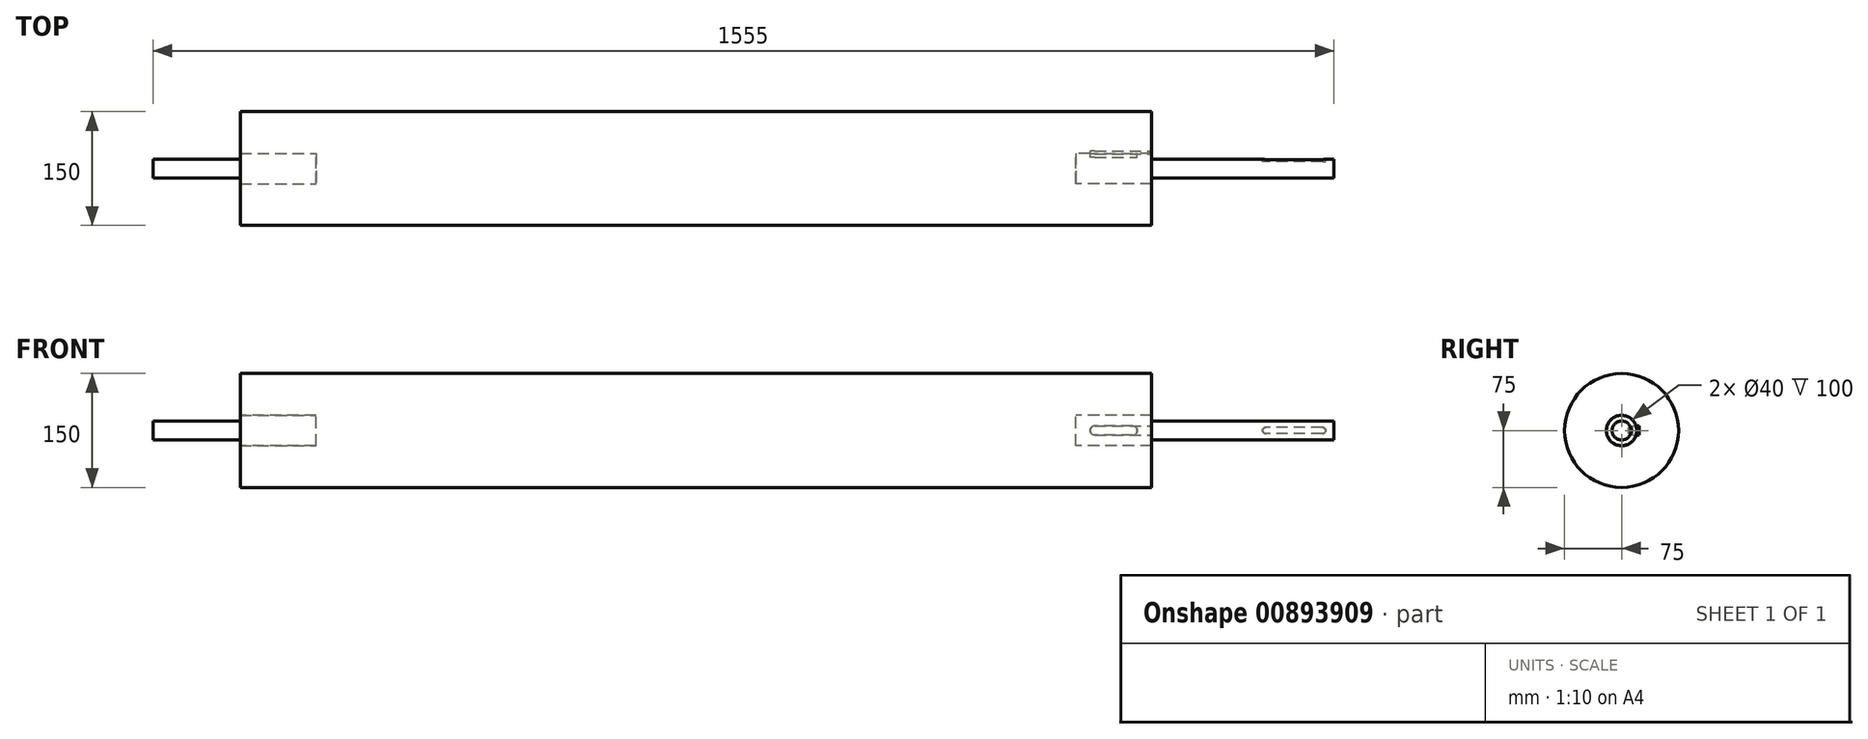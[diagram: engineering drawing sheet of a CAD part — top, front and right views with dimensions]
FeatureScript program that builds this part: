
annotation { "Feature Type Name" : "Feature", "Feature Type Description" : "" }
export const myFeature = defineFeature(function(context is Context, id is Id, definition is map)
    precondition{}
    {
        {
            var Q0;
            Q0=qCreatedBy(makeId("Right.planeOp"),FACE);
            var sketch = newSketch(context, id + "F0", { "sketchPlane" : qUnion([Q0])});
            skCircle(sketch, "E0", {"center": v(0, 0) * mm, "radius": 75 * mm});
            skSolve(sketch);
        }
        {
            var Q0;
            Q0 = qSketchRegion(id + "F0", true);
            extrude(context, id + "F1", {"entities" : qUnion([Q0]), "endBound" : BoundingType.SYMMETRIC, "depth" : 1200 * mm, "offsetDistance" : 25 * mm});
        }
        {
            var Q0;
            Q0=makeQuery(id+"F1.opExtrude","CAP_FACE",FACE,{"disambiguationData":[OSD([sQuery(id+"F0.wireOp",EDGE,"E0")])],"isStart":false});
            var sketch = newSketch(context, id + "F2", { "sketchPlane" : qUnion([Q0])});
            skCircle(sketch, "E1", {"center": v(0, 0) * mm, "radius": 20 * mm});
            skSolve(sketch);
        }
        {
            var Q0;
            Q0 = qSketchRegion(id + "F2", true);
            extrude(context, id + "F3", {"entities" : qUnion([Q0]), "operationType" : NewBodyOperationType.REMOVE, "oppositeDirection" : true, "depth" : 100 * mm, "offsetDistance" : 25 * mm});
        }
        {
            var Q0;
            Q0=makeQuery(id+"F1.opExtrude","CAP_FACE",FACE,{"disambiguationData":[OSD([sQuery(id+"F0.wireOp",EDGE,"E0")])],"isStart":true});
            var sketch = newSketch(context, id + "F4", { "sketchPlane" : qUnion([Q0])});
            skCircle(sketch, "E2", {"center": v(0, 0) * mm, "radius": 20 * mm});
            skSolve(sketch);
        }
        {
            var Q0;
            Q0 = qSketchRegion(id + "F4", true);
            extrude(context, id + "F5", {"entities" : qUnion([Q0]), "operationType" : NewBodyOperationType.REMOVE, "oppositeDirection" : true, "depth" : 100 * mm, "offsetDistance" : 25 * mm});
        }
        {
            var Q0;
            Q0=makeQuery(id+"F1.opExtrude","CAP_FACE",FACE,{"disambiguationData":[OSD([sQuery(id+"F0.wireOp",EDGE,"E0")])],"isStart":false});
            var sketch = newSketch(context, id + "F6", { "sketchPlane" : qUnion([Q0])});
            skLineSegment(sketch, "E3.bottom", {"start": v(19.08, 6) * mm, "end": v(23.3, 6) * mm});
            skLineSegment(sketch, "E3.top", {"start": v(19.08, -6) * mm, "end": v(23.3, -6) * mm});
            skLineSegment(sketch, "E3.left", {"start": v(19.08, 6) * mm, "end": v(19.08, -6) * mm});
            skLineSegment(sketch, "E3.right", {"start": v(23.3, 6) * mm, "end": v(23.3, -6) * mm});
            skPoint(sketch, "E3.middle", {"position": v(21.19, 0) * mm});
            skSolve(sketch);
        }
        {
            var Q0;
            Q0 = qSketchRegion(id + "F6", true);
            extrude(context, id + "F7", {"entities" : qUnion([Q0]), "operationType" : NewBodyOperationType.REMOVE, "oppositeDirection" : true, "depth" : 75 * mm, "offsetDistance" : 25 * mm});
        }
        {
            var Q0;
            Q0=makeQuery(id+"F3.boolean.opBoolean","COPY",FACE,{"derivedFrom":makeQuery(id+"F3.opExtrude","CAP_FACE",FACE,{"disambiguationData":[OSD([sQuery(id+"F2.wireOp",EDGE,"E1")])],"isStart":false})});
            var sketch = newSketch(context, id + "F8", { "sketchPlane" : qUnion([Q0])});
            skCircle(sketch, "E4", {"center": v(0, 0) * mm, "radius": 20 * mm});
            skSolve(sketch);
        }
        {
            var Q0;
            Q0 = qSketchRegion(id + "F8", true);
            extrude(context, id + "F9", {"entities" : qUnion([Q0]), "depth" : 100 * mm, "offsetDistance" : 25 * mm});
        }
        {
            var Q0;
            Q0=makeQuery(id+"F9.opExtrude","CAP_FACE",FACE,{"disambiguationData":[OSD([sQuery(id+"F8.wireOp",EDGE,"E4")])],"isStart":false});
            var sketch = newSketch(context, id + "F10", { "sketchPlane" : qUnion([Q0])});
            skCircle(sketch, "E5", {"center": v(0, 0) * mm, "radius": 12.5 * mm});
            skSolve(sketch);
        }
        {
            var Q0;
            Q0 = qSketchRegion(id + "F10", true);
            extrude(context, id + "F11", {"entities" : qUnion([Q0]), "operationType" : NewBodyOperationType.ADD, "depth" : 115 * mm, "offsetDistance" : 25 * mm});
        }
        {
            var Q0;
            Q0=makeQuery(id+"F9.opExtrude","SWEPT_BODY",BODY,{"disambiguationData":[OSD([sQuery(id+"F8.wireOp",EDGE,"E4")])]});
            var Q1;
            Q1=qCreatedBy(makeId("Right.planeOp"),FACE);
            mirror(context, id + "F12", {"entities" : qUnion([Q0]), "mirrorPlane" : qUnion([Q1])});
        }
        {
            var Q0;
            Q0=makeQuery(id+"F7.boolean.opBoolean","COPY",FACE,{"derivedFrom":makeQuery(id+"F7.opExtrude","SWEPT_FACE",FACE,{"disambiguationData":[OSD([sQuery(id+"F6.wireOp",EDGE,"E3.right")])]})});
            var sketch = newSketch(context, id + "F13", { "sketchPlane" : qUnion([Q0])});
            skLineSegment(sketch, "E6", {"start": v(525, 0) * mm, "end": v(575, 0) * mm});
            skArc(sketch, "E7.0.startCap", {"start": v(525, -6) * mm, "mid": v(519, 0) * mm, "end": v(525, 6) * mm});
            skArc(sketch, "E7.0.endCap", {"start": v(575, 6) * mm, "mid": v(581, 0) * mm, "end": v(575, -6) * mm});
            skLineSegment(sketch, "E7.0.left", {"start": v(525, 6) * mm, "end": v(575, 6) * mm});
            skLineSegment(sketch, "E7.0.right", {"start": v(525, -6) * mm, "end": v(575, -6) * mm});
            skSolve(sketch);
        }
        {
            var Q0;
            Q0 = qSketchRegion(id + "F13", true);
            extrude(context, id + "F14", {"entities" : qUnion([Q0]), "operationType" : NewBodyOperationType.REMOVE, "depth" : 8.8 * mm, "offsetDistance" : 25 * mm});
        }
        {
            var Q0;
            Q0=makeQuery(id+"F11.opExtrude","CAP_FACE",FACE,{"disambiguationData":[OSD([sQuery(id+"F10.wireOp",EDGE,"E5")])],"isStart":false});
            extrude(context, id + "F15", {"entities" : qUnion([Q0]), "operationType" : NewBodyOperationType.ADD, "depth" : 125 * mm, "offsetDistance" : 25 * mm});
        }
        {
            var Q0;
            Q0=qCreatedBy(makeId("Front.planeOp"),FACE);
            cPlane(context, id + "F16", {"entities" : qUnion([Q0]), "cplaneType" : CPlaneType.OFFSET, "offset" : 12.5 * mm, "oppositeDirection" : true, "width" : 150 * mm, "height" : 150 * mm});
        }
        {
            var Q0;
            Q0=qCreatedBy(id+"F16.planeOp",FACE);
            var sketch = newSketch(context, id + "F17", { "sketchPlane" : qUnion([Q0])});
            skLineSegment(sketch, "E8", {"start": v(825, 0) * mm, "end": v(750, 0) * mm});
            skArc(sketch, "E9.0.startCap", {"start": v(825, 4) * mm, "mid": v(829, 0) * mm, "end": v(825, -4) * mm});
            skArc(sketch, "E9.0.endCap", {"start": v(750, -4) * mm, "mid": v(746, 0) * mm, "end": v(750, 4) * mm});
            skLineSegment(sketch, "E9.0.left", {"start": v(825, -4) * mm, "end": v(750, -4) * mm});
            skLineSegment(sketch, "E9.0.right", {"start": v(825, 4) * mm, "end": v(750, 4) * mm});
            skSolve(sketch);
        }
        {
            var Q0;
            Q0 = qSketchRegion(id + "F17", true);
            extrude(context, id + "F18", {"entities" : qUnion([Q0]), "operationType" : NewBodyOperationType.REMOVE, "depth" : 3.3 * mm, "offsetDistance" : 25 * mm});
        }
    });
